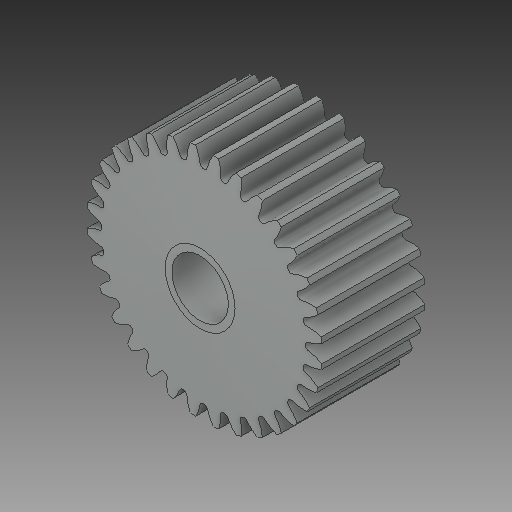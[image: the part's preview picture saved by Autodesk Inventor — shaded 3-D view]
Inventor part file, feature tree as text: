
AUTODESK INVENTOR PART (.ipt)
format: ipt  version: 2017 SP1 (Build 210196100, 196)  size: 509,952 bytes
history: native  units: in
note: dims shown in document units (in); Inventor stores cm internally (conversion verified against a paired STEP export)
features: mirror x1
ambient origin geometry x8: Origin, YZ Plane, XZ Plane, XY Plane, X Axis, Y Axis, Z Axis, Center Point
bodies: Solid1 (feature_tree)
feature tree (1):
  mirror  "Mirror1"
